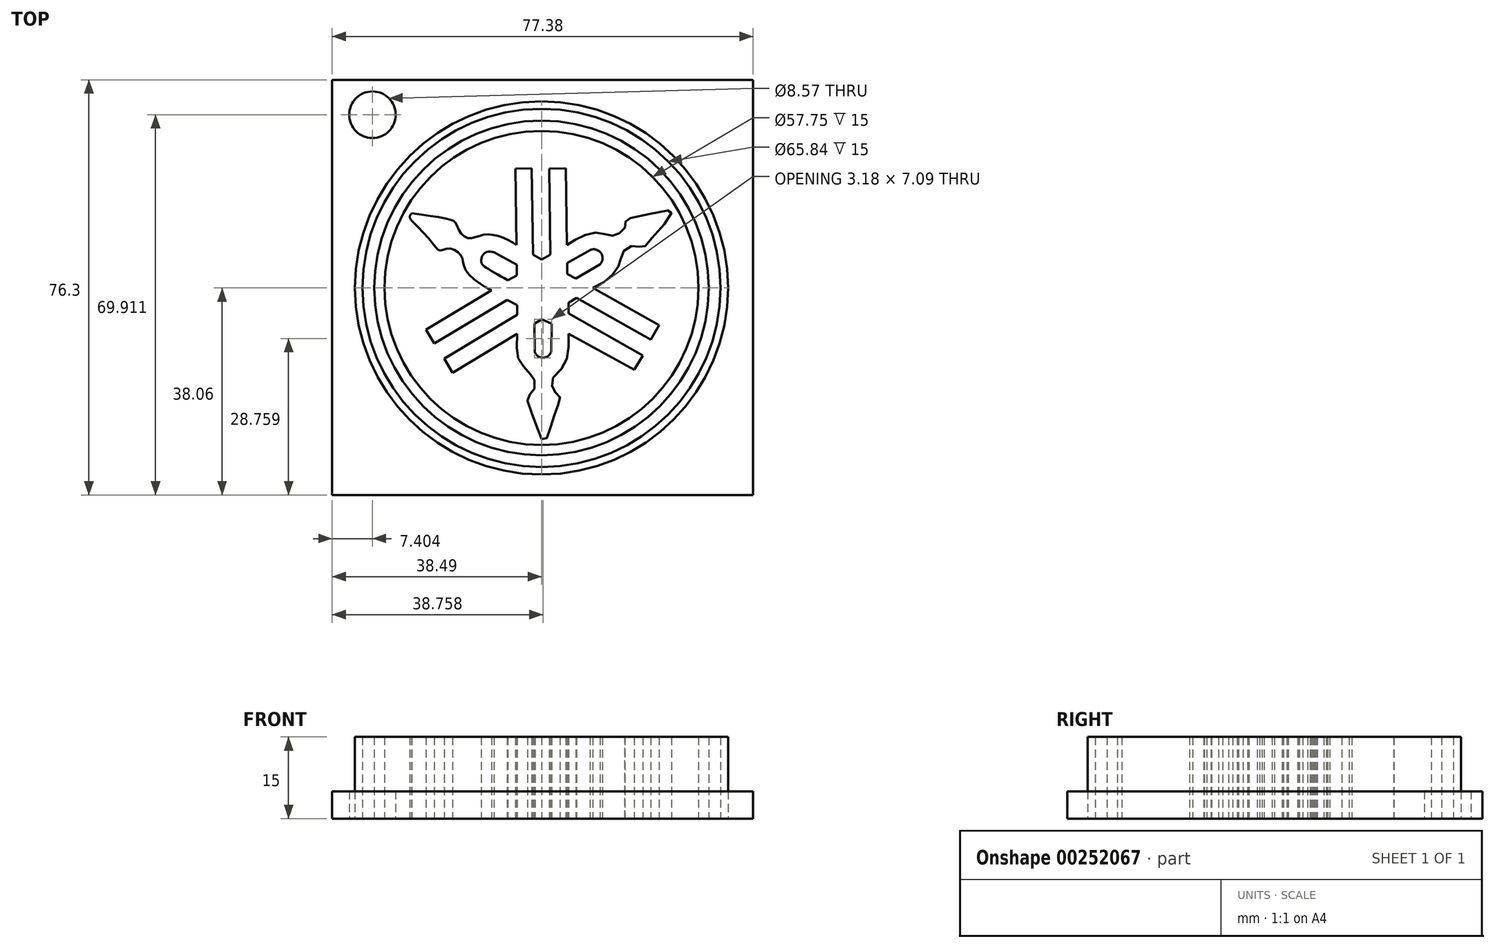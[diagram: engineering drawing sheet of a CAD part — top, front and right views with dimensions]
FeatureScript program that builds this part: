
annotation { "Feature Type Name" : "Feature", "Feature Type Description" : "" }
export const myFeature = defineFeature(function(context is Context, id is Id, definition is map)
    precondition{}
    {
        {
            var Q0;
            Q0=qCreatedBy(makeId("Top.planeOp"),FACE);
            var sketch = newSketch(context, id + "F0", { "sketchPlane" : qUnion([Q0])});
            skFitSpline(sketch, "E0", {"points": [v(-23.88, 12.43) * mm, v(-19.99, 8.19) * mm, v(-19.04, 7.04) * mm, v(-18.4, 6.89) * mm, v(-17.3, 7.24) * mm, v(-15.7, 6.84) * mm, v(-14.6, 5.6) * mm, v(-14.4, 4.54) * mm, v(-13.4, 2.55) * mm, v(-10.06, 0) * mm, v(-9.16, -0.45) * mm], "startDerivative": vector(26.17, -27.18) * mm, "endDerivative": vector(9.8, -4.27) * mm});
            skLineSegment(sketch, "E1", {"start": v(-9.16, -0.45) * mm, "end": v(-21.24, -7.68) * mm});
            skLineSegment(sketch, "E2", {"start": v(-21.24, -7.68) * mm, "end": v(-19.7, -10.24) * mm});
            skLineSegment(sketch, "E3", {"start": v(-19.7, -10.24) * mm, "end": v(-6.34, -2.23) * mm});
            skLineSegment(sketch, "E4", {"start": v(-6.34, -2.23) * mm, "end": v(-4.47, -3.14) * mm});
            skLineSegment(sketch, "E5", {"start": v(-4.47, -3.14) * mm, "end": v(-4.47, -4.94) * mm});
            skLineSegment(sketch, "E6", {"start": v(-4.47, -4.94) * mm, "end": v(-17.9, -13.02) * mm});
            skLineSegment(sketch, "E7", {"start": v(-17.9, -13.02) * mm, "end": v(-16.35, -15.59) * mm});
            skLineSegment(sketch, "E8", {"start": v(-16.35, -15.59) * mm, "end": v(-4.47, -8.43) * mm});
            skFitSpline(sketch, "E9", {"points": [v(-4.47, -8.43) * mm, v(-4.47, -12.17) * mm, v(-3.8, -13.77) * mm, v(-2.2, -15.77) * mm, v(-1.49, -16.48) * mm, v(-1.17, -17.86) * mm, v(-1.75, -19.28) * mm, v(-2.46, -19.9) * mm, v(-2.46, -21.06) * mm, v(-0.64, -26) * mm, v(0.16, -27.93) * mm, v(0.78, -27.87) * mm, v(1.66, -25.55) * mm, v(2.7, -22.41) * mm, v(3.33, -20.67) * mm, v(3.32, -19.92) * mm, v(2.51, -19.15) * mm, v(1.96, -18.13) * mm, v(2, -16.76) * mm, v(3.9, -14.6) * mm, v(4.89, -11.83) * mm, v(4.99, -8.43) * mm], "startDerivative": vector(-3.37, -63.26) * mm, "endDerivative": vector(-0.73, 54.6) * mm});
            skLineSegment(sketch, "E10", {"start": v(4.99, -8.43) * mm, "end": v(17.08, -15.03) * mm});
            skLineSegment(sketch, "E11", {"start": v(17.08, -15.03) * mm, "end": v(18.66, -12.45) * mm});
            skLineSegment(sketch, "E12", {"start": v(18.66, -12.45) * mm, "end": v(4.99, -4.7) * mm});
            skLineSegment(sketch, "E13", {"start": v(4.99, -4.7) * mm, "end": v(4.99, -2.73) * mm});
            skLineSegment(sketch, "E14", {"start": v(4.99, -2.73) * mm, "end": v(6.44, -1.85) * mm});
            skLineSegment(sketch, "E15", {"start": v(6.44, -1.85) * mm, "end": v(20.09, -9.51) * mm});
            skLineSegment(sketch, "E16", {"start": v(20.09, -9.51) * mm, "end": v(21.6, -6.83) * mm});
            skLineSegment(sketch, "E17", {"start": v(21.6, -6.83) * mm, "end": v(9.43, 0) * mm});
            skFitSpline(sketch, "E18", {"points": [v(9.43, 0) * mm, v(12.16, 1.54) * mm, v(13.7, 3.26) * mm, v(14.48, 4.74) * mm, v(14.7, 5.98) * mm, v(15.58, 7.26) * mm, v(17.12, 7.75) * mm, v(18.2, 7.52) * mm, v(18.93, 7.6) * mm, v(19.98, 8.81) * mm, v(23.76, 13.34) * mm, v(23.8, 14.14) * mm, v(23.12, 14.23) * mm, v(16.13, 12.75) * mm, v(15.61, 12.45) * mm, v(15.36, 11.81) * mm, v(15.29, 11.01) * mm, v(14.44, 10.13) * mm, v(13.37, 9.6) * mm, v(11.92, 9.8) * mm, v(10.58, 10.14) * mm, v(8.63, 9.91) * mm, v(6.31, 8.88) * mm, v(4.67, 7.91) * mm], "startDerivative": vector(49.67, 23.64) * mm, "endDerivative": vector(-33.34, -20.56) * mm});
            skLineSegment(sketch, "E19", {"start": v(4.67, 7.91) * mm, "end": v(4.5, 21.98) * mm});
            skLineSegment(sketch, "E20", {"start": v(4.5, 21.98) * mm, "end": v(1.4, 21.94) * mm});
            skLineSegment(sketch, "E21", {"start": v(1.4, 21.94) * mm, "end": v(1.6, 6.12) * mm});
            skLineSegment(sketch, "E22", {"start": v(0, 5.23) * mm, "end": v(1.6, 6.12) * mm});
            skLineSegment(sketch, "E23", {"start": v(-1.59, 6.12) * mm, "end": v(0, 5.23) * mm});
            skLineSegment(sketch, "E24", {"start": v(-1.59, 6.12) * mm, "end": v(-1.79, 21.98) * mm});
            skLineSegment(sketch, "E25", {"start": v(-1.79, 21.98) * mm, "end": v(-4.8, 21.94) * mm});
            skLineSegment(sketch, "E26", {"start": v(-4.8, 21.94) * mm, "end": v(-4.61, 7.91) * mm});
            skFitSpline(sketch, "E27", {"points": [v(-4.61, 7.91) * mm, v(-7.49, 9.39) * mm, v(-10.66, 9.77) * mm, v(-12.84, 9.15) * mm, v(-14.63, 9.8) * mm, v(-15.77, 11.88) * mm, v(-16.49, 12.47) * mm, v(-23.82, 13.73) * mm], "startDerivative": vector(-17.86, 10.8) * mm, "endDerivative": vector(-39.94, 5.63) * mm});
            skArc(sketch, "E28", {"start": v(-23.82, 13.73) * mm, "mid": v(-24.2, 13.1) * mm, "end": v(-23.88, 12.43) * mm});
            skFitSpline(sketch, "E29", {"points": [v(-6.17, 1.43) * mm, v(-10.37, 3.86) * mm, v(-11.01, 4.61) * mm, v(-10.92, 5.8) * mm, v(-10.07, 6.63) * mm, v(-8.72, 6.58) * mm], "startDerivative": vector(-15.07, 8.29) * mm, "endDerivative": vector(8.03, -1.53) * mm});
            skLineSegment(sketch, "E30", {"start": v(-8.72, 6.58) * mm, "end": v(-4.53, 4.27) * mm});
            skLineSegment(sketch, "E31", {"start": v(-4.53, 4.27) * mm, "end": v(-4.53, 2.32) * mm});
            skLineSegment(sketch, "E32", {"start": v(-4.53, 2.32) * mm, "end": v(-6.17, 1.43) * mm});
            skLineSegment(sketch, "E33", {"start": v(-1.73, 0.9) * mm, "end": v(-1.73, -1.26) * mm});
            skLineSegment(sketch, "E34", {"start": v(-1.73, -1.26) * mm, "end": v(0, -2.32) * mm});
            skLineSegment(sketch, "E35", {"start": v(0, -2.32) * mm, "end": v(1.92, -1.16) * mm});
            skLineSegment(sketch, "E36", {"start": v(1.92, -1.16) * mm, "end": v(1.85, 0.8) * mm});
            skLineSegment(sketch, "E37", {"start": v(1.85, 0.8) * mm, "end": v(0.25, 1.9) * mm});
            skLineSegment(sketch, "E38", {"start": v(0.25, 1.9) * mm, "end": v(-1.73, 0.88) * mm});
            skArc(sketch, "E39", {"start": v(10.78, 4.35) * mm, "mid": v(10.93, 6.43) * mm, "end": v(8.91, 6.95) * mm});
            skLineSegment(sketch, "E40", {"start": v(8.91, 6.95) * mm, "end": v(4.73, 4.57) * mm});
            skLineSegment(sketch, "E41", {"start": v(4.73, 4.57) * mm, "end": v(4.73, 2.59) * mm});
            skLineSegment(sketch, "E42", {"start": v(4.73, 2.59) * mm, "end": v(6.33, 1.7) * mm});
            skLineSegment(sketch, "E43", {"start": v(6.33, 1.7) * mm, "end": v(10.78, 4.35) * mm});
            skCircle(sketch, "E44", {"center": v(0, 0) * mm, "radius": 28.87 * mm});
            skArc(sketch, "E45", {"start": v(-1.25, -11.68) * mm, "mid": v(0.33, -12.85) * mm, "end": v(1.81, -11.56) * mm});
            skLineSegment(sketch, "E46", {"start": v(-1.32, -6.57) * mm, "end": v(-1.25, -11.68) * mm});
            skLineSegment(sketch, "E47", {"start": v(-1.32, -6.57) * mm, "end": v(0, -5.76) * mm});
            skLineSegment(sketch, "E48", {"start": v(0, -5.76) * mm, "end": v(1.86, -6.57) * mm});
            skLineSegment(sketch, "E49", {"start": v(1.86, -6.57) * mm, "end": v(1.81, -11.56) * mm});
            skCircle(sketch, "E50", {"center": v(0, 0) * mm, "radius": 34.3 * mm});
            skCircle(sketch, "E51", {"center": v(0, 0) * mm, "radius": 32.92 * mm});
            skCircle(sketch, "E52", {"center": v(0, 0) * mm, "radius": 30.76 * mm});
            skSolve(sketch);
        }
        {
            var Q0;
            Q0=makeQuery(id+"F0.imprint","IMPRINT",FACE,{"disambiguationData":[TD([[makeQuery(id+"F0.imprint","IMPRINT",EDGE,{"derivedFrom":sQuery(id+"F0.wireOp",EDGE,"E0")}),1.0]])]});
            var Q1;
            Q1=makeQuery(id+"F0.imprint","IMPRINT",FACE,{"disambiguationData":[TD([[makeQuery(id+"F0.imprint","IMPRINT",EDGE,{"derivedFrom":sQuery(id+"F0.wireOp",EDGE,"E50")}),1.0]])]});
            var Q2;
            Q2=makeQuery(id+"F0.imprint","IMPRINT",FACE,{"disambiguationData":[TD([[makeQuery(id+"F0.imprint","IMPRINT",EDGE,{"derivedFrom":sQuery(id+"F0.wireOp",EDGE,"E44")}),-1.0]])]});
            extrude(context, id + "F1", {"entities" : qUnion([Q0, Q1, Q2]), "offsetDistance" : 25 * mm, "depth" : 15 * mm});
        }
        {
            var Q0;
            Q0=qCreatedBy(makeId("Top.planeOp"),FACE);
            var sketch = newSketch(context, id + "F2", { "sketchPlane" : qUnion([Q0])});
            skLineSegment(sketch, "E53.bottom", {"start": v(-38.49, 38.24) * mm, "end": v(38.89, 38.24) * mm});
            skLineSegment(sketch, "E53.top", {"start": v(-38.49, -38.06) * mm, "end": v(38.89, -38.06) * mm});
            skLineSegment(sketch, "E53.left", {"start": v(-38.49, 38.24) * mm, "end": v(-38.49, -38.06) * mm});
            skLineSegment(sketch, "E53.right", {"start": v(38.89, 38.24) * mm, "end": v(38.89, -38.06) * mm});
            skCircle(sketch, "E54", {"center": v(-31.09, 31.85) * mm, "radius": 4.28 * mm});
            skSolve(sketch);
        }
        {
            var Q0;
            Q0=makeQuery(id+"F2.imprint","IMPRINT",FACE,{"disambiguationData":[TD([[makeQuery(id+"F2.imprint","IMPRINT",EDGE,{"derivedFrom":sQuery(id+"F2.wireOp",EDGE,"E53.bottom")}),-1.0]])]});
            extrude(context, id + "F3", {"entities" : qUnion([Q0]), "depth" : 5 * mm, "offsetDistance" : 25 * mm});
        }
    });
